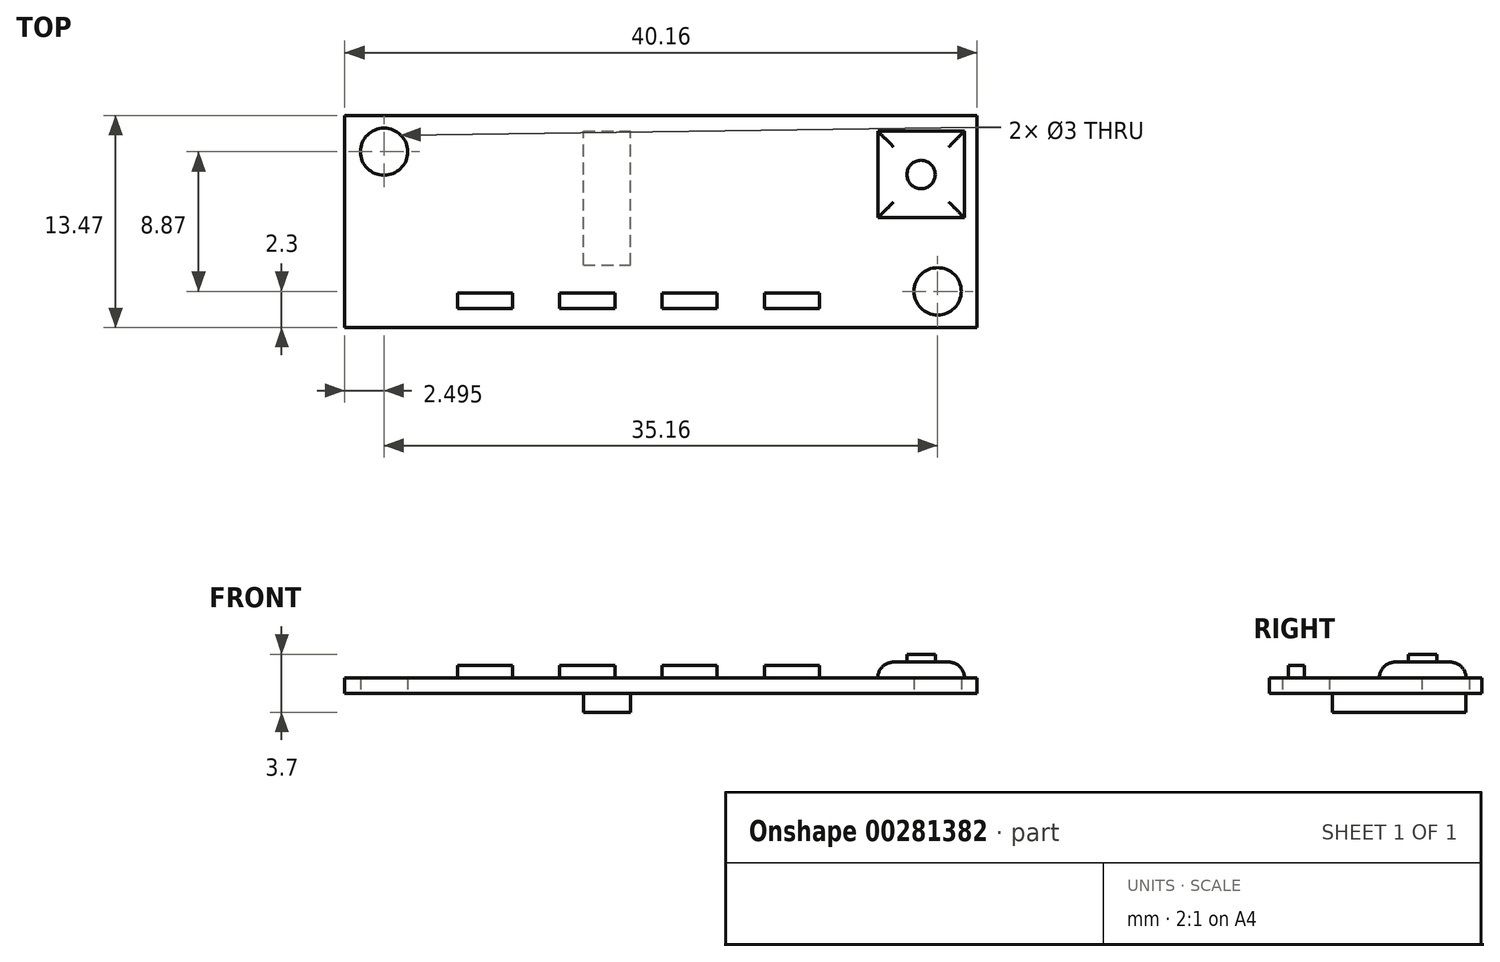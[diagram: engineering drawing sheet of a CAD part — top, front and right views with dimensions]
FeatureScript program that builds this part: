
annotation { "Feature Type Name" : "Feature", "Feature Type Description" : "" }
export const myFeature = defineFeature(function(context is Context, id is Id, definition is map)
    precondition{}
    {
        {
            var Q0;
            Q0=qCreatedBy(makeId("Top.planeOp"),FACE);
            var sketch = newSketch(context, id + "F0", { "sketchPlane" : qUnion([Q0])});
            skLineSegment(sketch, "E0.bottom", {"start": v(-18.17, 10.05) * mm, "end": v(21.99, 10.05) * mm});
            skLineSegment(sketch, "E0.top", {"start": v(-18.17, -3.42) * mm, "end": v(21.99, -3.42) * mm});
            skLineSegment(sketch, "E0.left", {"start": v(-18.17, 10.05) * mm, "end": v(-18.17, -3.42) * mm});
            skLineSegment(sketch, "E0.right", {"start": v(21.99, 10.05) * mm, "end": v(21.99, -3.42) * mm});
            skLineSegment(sketch, "E1.bottom", {"start": v(15.69, 9.05) * mm, "end": v(21.19, 9.05) * mm});
            skLineSegment(sketch, "E1.top", {"start": v(15.69, 3.55) * mm, "end": v(21.19, 3.55) * mm});
            skLineSegment(sketch, "E1.left", {"start": v(15.69, 9.05) * mm, "end": v(15.69, 3.55) * mm});
            skLineSegment(sketch, "E1.right", {"start": v(21.19, 9.05) * mm, "end": v(21.19, 3.55) * mm});
            skCircle(sketch, "E2", {"center": v(19.49, -1.12) * mm, "radius": 1.5 * mm});
            skCircle(sketch, "E3", {"center": v(-15.67, 7.75) * mm, "radius": 1.5 * mm});
            skLineSegment(sketch, "E4.bottom", {"start": v(8.49, -1.22) * mm, "end": v(11.99, -1.22) * mm});
            skLineSegment(sketch, "E4.top", {"start": v(8.49, -2.22) * mm, "end": v(11.99, -2.22) * mm});
            skLineSegment(sketch, "E4.left", {"start": v(8.49, -1.22) * mm, "end": v(8.49, -2.22) * mm});
            skLineSegment(sketch, "E4.right", {"start": v(11.99, -1.22) * mm, "end": v(11.99, -2.22) * mm});
            skLineSegment(sketch, "E5.bottom", {"start": v(1.99, -1.22) * mm, "end": v(5.49, -1.22) * mm});
            skLineSegment(sketch, "E5.top", {"start": v(1.99, -2.22) * mm, "end": v(5.49, -2.22) * mm});
            skLineSegment(sketch, "E5.left", {"start": v(1.99, -1.22) * mm, "end": v(1.99, -2.22) * mm});
            skLineSegment(sketch, "E5.right", {"start": v(5.49, -1.22) * mm, "end": v(5.49, -2.22) * mm});
            skPoint(sketch, "E6.oppositeSnap0", {"position": v(3.74, -2.22) * mm});
            skLineSegment(sketch, "E6.bottom", {"start": v(-4.51, -1.22) * mm, "end": v(-1.01, -1.22) * mm});
            skLineSegment(sketch, "E6.top", {"start": v(-4.51, -2.22) * mm, "end": v(-1.01, -2.22) * mm});
            skLineSegment(sketch, "E6.left", {"start": v(-4.51, -1.22) * mm, "end": v(-4.51, -2.22) * mm});
            skLineSegment(sketch, "E6.right", {"start": v(-1.01, -1.22) * mm, "end": v(-1.01, -2.22) * mm});
            skLineSegment(sketch, "E7.bottom", {"start": v(-11.01, -1.22) * mm, "end": v(-7.51, -1.22) * mm});
            skLineSegment(sketch, "E7.top", {"start": v(-11.01, -2.22) * mm, "end": v(-7.51, -2.22) * mm});
            skLineSegment(sketch, "E7.left", {"start": v(-11.01, -1.22) * mm, "end": v(-11.01, -2.22) * mm});
            skLineSegment(sketch, "E7.right", {"start": v(-7.51, -1.22) * mm, "end": v(-7.51, -2.22) * mm});
            skSolve(sketch);
        }
        {
            var Q0;
            Q0 = qSketchRegion(id + "F0", true);
            var Q1;
            Q1=makeQuery(id+"F0.imprint","IMPRINT",FACE,{"disambiguationData":[TD([[makeQuery(id+"F0.imprint","IMPRINT",EDGE,{"derivedFrom":sQuery(id+"F0.wireOp",EDGE,"E7.bottom")}),-1.0]])]});
            var Q2;
            Q2=makeQuery(id+"F0.imprint","IMPRINT",FACE,{"disambiguationData":[TD([[makeQuery(id+"F0.imprint","IMPRINT",EDGE,{"derivedFrom":sQuery(id+"F0.wireOp",EDGE,"E6.bottom")}),-1.0]])]});
            var Q3;
            Q3=makeQuery(id+"F0.imprint","IMPRINT",FACE,{"disambiguationData":[TD([[makeQuery(id+"F0.imprint","IMPRINT",EDGE,{"derivedFrom":sQuery(id+"F0.wireOp",EDGE,"E5.bottom")}),-1.0]])]});
            var Q4;
            Q4=makeQuery(id+"F0.imprint","IMPRINT",FACE,{"disambiguationData":[TD([[makeQuery(id+"F0.imprint","IMPRINT",EDGE,{"derivedFrom":sQuery(id+"F0.wireOp",EDGE,"E4.bottom")}),-1.0]])]});
            var Q5;
            Q5=makeQuery(id+"F0.imprint","IMPRINT",FACE,{"disambiguationData":[TD([[makeQuery(id+"F0.imprint","IMPRINT",EDGE,{"derivedFrom":sQuery(id+"F0.wireOp",EDGE,"E1.bottom")}),-1.0]])]});
            extrude(context, id + "F1", {"entities" : qUnion([Q0, Q1, Q2, Q3, Q4, Q5]), "depth" : 1 * mm});
        }
        {
            var Q0;
            Q0=makeQuery(id+"F0.imprint","IMPRINT",FACE,{"disambiguationData":[TD([[makeQuery(id+"F0.imprint","IMPRINT",EDGE,{"derivedFrom":sQuery(id+"F0.wireOp",EDGE,"E7.bottom")}),-1.0]])]});
            var Q1;
            Q1=makeQuery(id+"F0.imprint","IMPRINT",FACE,{"disambiguationData":[TD([[makeQuery(id+"F0.imprint","IMPRINT",EDGE,{"derivedFrom":sQuery(id+"F0.wireOp",EDGE,"E6.bottom")}),-1.0]])]});
            var Q2;
            Q2=makeQuery(id+"F0.imprint","IMPRINT",FACE,{"disambiguationData":[TD([[makeQuery(id+"F0.imprint","IMPRINT",EDGE,{"derivedFrom":sQuery(id+"F0.wireOp",EDGE,"E5.bottom")}),-1.0]])]});
            var Q3;
            Q3=makeQuery(id+"F0.imprint","IMPRINT",FACE,{"disambiguationData":[TD([[makeQuery(id+"F0.imprint","IMPRINT",EDGE,{"derivedFrom":sQuery(id+"F0.wireOp",EDGE,"E4.bottom")}),-1.0]])]});
            extrude(context, id + "F2", {"entities" : qUnion([Q0, Q1, Q2, Q3]), "operationType" : NewBodyOperationType.ADD, "depth" : 1.8 * mm});
        }
        {
            var Q0;
            Q0=makeQuery(id+"F0.imprint","IMPRINT",FACE,{"disambiguationData":[TD([[makeQuery(id+"F0.imprint","IMPRINT",EDGE,{"derivedFrom":sQuery(id+"F0.wireOp",EDGE,"E1.bottom")}),-1.0]])]});
            extrude(context, id + "F3", {"entities" : qUnion([Q0]), "operationType" : NewBodyOperationType.ADD, "depth" : 2 * mm});
        }
        {
            var Q0;
            Q0=makeQuery(id+"F3.opExtrude","CAP_EDGE",EDGE,{"disambiguationData":[OSD([sQuery(id+"F0.wireOp",EDGE,"E1.right")])],"isStart":false});
            var Q1;
            Q1=makeQuery(id+"F3.opExtrude","CAP_EDGE",EDGE,{"disambiguationData":[OSD([sQuery(id+"F0.wireOp",EDGE,"E1.left")])],"isStart":false});
            var Q2;
            Q2=makeQuery(id+"F3.opExtrude","CAP_EDGE",EDGE,{"disambiguationData":[OSD([sQuery(id+"F0.wireOp",EDGE,"E1.top")])],"isStart":false});
            var Q3;
            Q3=makeQuery(id+"F3.opExtrude","CAP_EDGE",EDGE,{"disambiguationData":[OSD([sQuery(id+"F0.wireOp",EDGE,"E1.bottom")])],"isStart":false});
            fillet(context, id + "F4", {"entities" : qUnion([Q0, Q1, Q2, Q3]), "radius" : 1 * mm, "tangentPropagation" : true, "allowEdgeOverflow" : false});
        }
        {
            var Q0;
            Q0=makeQuery(id+"F3.opExtrude","CAP_FACE",FACE,{"disambiguationData":[OSD([sQuery(id+"F0.wireOp",EDGE,"E1.bottom"),sQuery(id+"F0.wireOp",EDGE,"E1.top"),sQuery(id+"F0.wireOp",EDGE,"E1.left"),sQuery(id+"F0.wireOp",EDGE,"E1.right")])],"isStart":false});
            var sketch = newSketch(context, id + "F5", { "sketchPlane" : qUnion([Q0])});
            skCircle(sketch, "E8", {"center": v(18.44, 6.3) * mm, "radius": 0.9 * mm});
            skSolve(sketch);
        }
        {
            var Q0;
            Q0=makeQuery(id+"F5.imprint","IMPRINT",FACE,{"disambiguationData":[TD([[makeQuery(id+"F5.imprint","IMPRINT",EDGE,{"derivedFrom":sQuery(id+"F5.wireOp",EDGE,"E8")}),1.0]])]});
            var Q1;
            Q1=sQuery(id+"F5.wireOp",EDGE,"E8");
            extrude(context, id + "F6", {"entities" : qUnion([Q0]), "operationType" : NewBodyOperationType.ADD, "surfaceEntities" : qUnion([Q1]), "depth" : 0.5 * mm});
        }
        {
            var Q0;
            Q0=makeQuery(id+"F1.opExtrude","CAP_FACE",FACE,{"disambiguationData":[OSD([sQuery(id+"F0.wireOp",EDGE,"E0.bottom"),sQuery(id+"F0.wireOp",EDGE,"E0.top"),sQuery(id+"F0.wireOp",EDGE,"E0.left"),sQuery(id+"F0.wireOp",EDGE,"E0.right"),sQuery(id+"F0.wireOp",EDGE,"E2"),sQuery(id+"F0.wireOp",EDGE,"E3")])],"isStart":true});
            var sketch = newSketch(context, id + "F7", { "sketchPlane" : qUnion([Q0])});
            skLineSegment(sketch, "E9.bottom", {"start": v(-3.01, -0.55) * mm, "end": v(-0.01, -0.55) * mm});
            skLineSegment(sketch, "E9.top", {"start": v(-3.01, -9.05) * mm, "end": v(-0.01, -9.05) * mm});
            skLineSegment(sketch, "E9.left", {"start": v(-3.01, -0.55) * mm, "end": v(-3.01, -9.05) * mm});
            skLineSegment(sketch, "E9.right", {"start": v(-0.01, -0.55) * mm, "end": v(-0.01, -9.05) * mm});
            skSolve(sketch);
        }
        {
            var Q0;
            Q0=makeQuery(id+"F7.imprint","IMPRINT",FACE,{"disambiguationData":[TD([[makeQuery(id+"F7.imprint","IMPRINT",EDGE,{"derivedFrom":sQuery(id+"F7.wireOp",EDGE,"E9.bottom")}),-1.0]])]});
            extrude(context, id + "F8", {"entities" : qUnion([Q0]), "operationType" : NewBodyOperationType.ADD, "depth" : 1.2 * mm});
        }
    });
